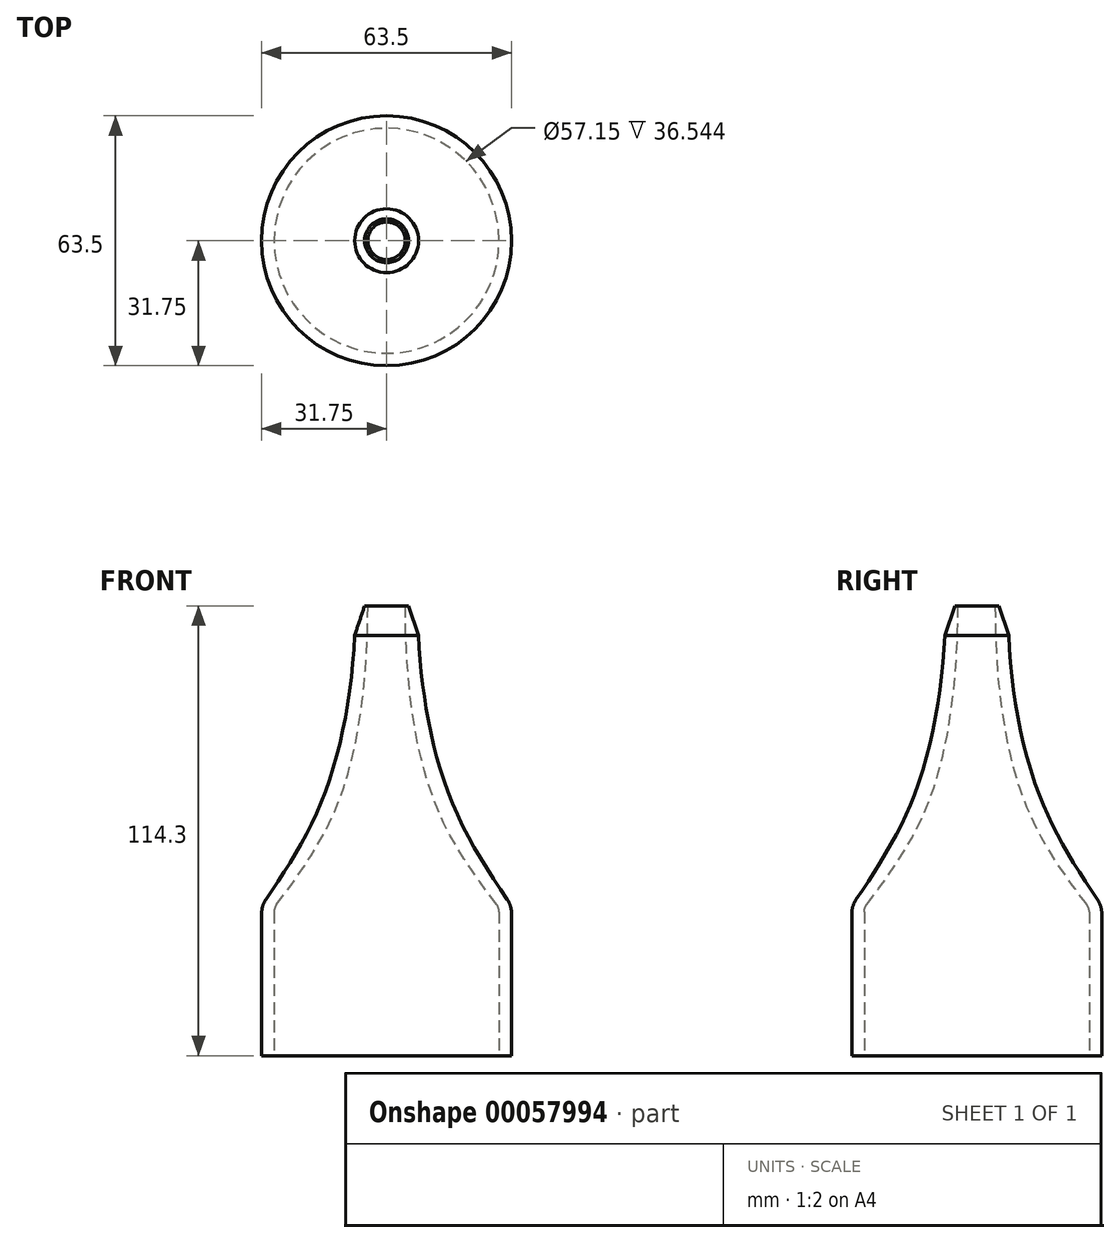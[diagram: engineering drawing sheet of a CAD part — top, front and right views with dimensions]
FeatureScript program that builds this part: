
annotation { "Feature Type Name" : "Feature", "Feature Type Description" : "" }
export const myFeature = defineFeature(function(context is Context, id is Id, definition is map)
    precondition{}
    {
        {
            var Q0;
            Q0=qCreatedBy(makeId("Front.planeOp"),FACE);
            var sketch = newSketch(context, id + "F0", { "sketchPlane" : qUnion([Q0])});
            skLineSegment(sketch, "E0", {"start": v(0, 0) * mm, "end": v(0, 114.3) * mm, "construction": true});
            skLineSegment(sketch, "E1", {"start": v(28.58, 0) * mm, "end": v(28.58, 37.62) * mm});
            skLineSegment(sketch, "E2", {"start": v(0, 114.3) * mm, "end": v(4.76, 114.3) * mm, "construction": true});
            skLineSegment(sketch, "E3", {"start": v(28.58, 0) * mm, "end": v(31.75, 0) * mm});
            skLineSegment(sketch, "E4", {"start": v(31.75, 0) * mm, "end": v(31.75, 38.1) * mm});
            skLineSegment(sketch, "E5", {"start": v(7.94, 114.3) * mm, "end": v(4.76, 114.3) * mm});
            skLineSegment(sketch, "E6", {"start": v(0, 114.3) * mm, "end": v(-4.76, 114.3) * mm, "construction": true});
            skLineSegment(sketch, "E7", {"start": v(28.58, 0) * mm, "end": v(0, 0) * mm, "construction": true});
            skLineSegment(sketch, "E8", {"start": v(0, 0) * mm, "end": v(-28.58, 0) * mm, "construction": true});
            skFitSpline(sketch, "E9", {"points": [v(28.58, 37.62) * mm, v(11.92, 65.24) * mm, v(4.76, 114.3) * mm], "startDerivative": vector(-42.76, 55.89) * mm, "endDerivative": vector(0, 96.24) * mm});
            skLineSegment(sketch, "E10", {"start": v(4.76, 114.3) * mm, "end": v(4.76, 122.66) * mm, "construction": true});
            skFitSpline(sketch, "E11", {"points": [v(31.75, 38.1) * mm, v(15.5, 67.29) * mm, v(7.94, 114.3) * mm], "startDerivative": vector(-40.68, 58.93) * mm, "endDerivative": vector(0, 92.8) * mm});
            skLineSegment(sketch, "E12", {"start": v(7.94, 114.3) * mm, "end": v(7.94, 122.74) * mm, "construction": true});
            skSolve(sketch);
        }
        {
            var Q0;
            Q0 = qSketchRegion(id + "F0", true);
            var Q1;
            Q1=sQuery(id+"F0.wireOp",EDGE,"E0");
            revolve(context, id + "F1", {"entities" : qUnion([Q0]), "axis" : qUnion([Q1]), "revolveType" : RevolveType.FULL});
        }
        {
            var Q0;
            Q0=makeQuery(id+"F1.opRevolve","SWEPT_EDGE",EDGE,{"disambiguationData":[OSD([sQuery(id+"F0.wireOp",EDGE,"E4"),sQuery(id+"F0.wireOp",EDGE,"E11")])]});
            fillet(context, id + "F2", {"entities" : qUnion([Q0]), "radius" : 6.35 * mm, "tangentPropagation" : true, "allowEdgeOverflow" : false});
        }
        {
            var Q0;
            Q0=makeQuery(id+"F1.opRevolve","SWEPT_EDGE",EDGE,{"disambiguationData":[OSD([sQuery(id+"F0.wireOp",EDGE,"E1"),sQuery(id+"F0.wireOp",EDGE,"E9")])]});
            fillet(context, id + "F3", {"entities" : qUnion([Q0]), "radius" : 3.17 * mm, "tangentPropagation" : true, "allowEdgeOverflow" : false});
        }
        {
            var Q0;
            Q0=makeQuery(id+"F1.opRevolve","SWEPT_EDGE",EDGE,{"disambiguationData":[OSD([sQuery(id+"F0.wireOp",EDGE,"E5"),sQuery(id+"F0.wireOp",EDGE,"E11")])]});
            chamfer(context, id + "F4", {"entities" : qUnion([Q0]), "chamferType" : ChamferType.TWO_OFFSETS, "width1" : 7.62 * mm, "oppositeDirection" : false, "width2" : 2.54 * mm, "tangentPropagation" : true});
        }
    });
